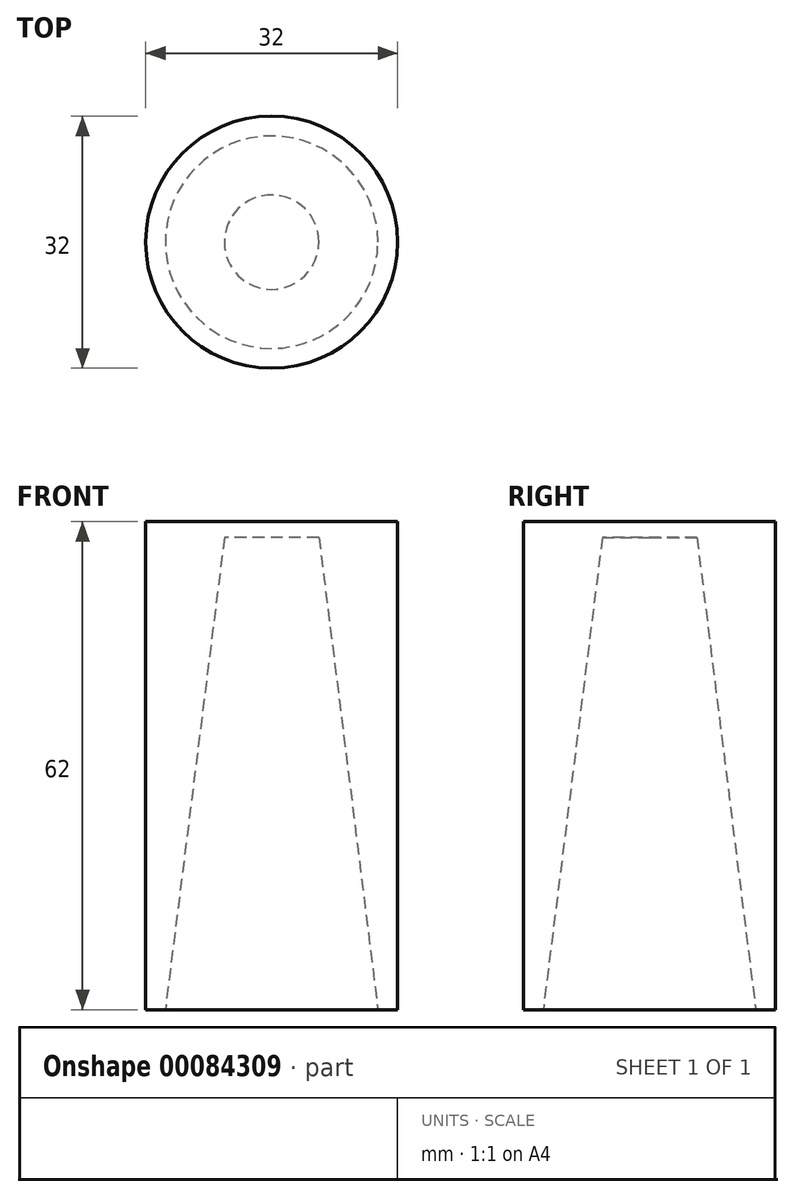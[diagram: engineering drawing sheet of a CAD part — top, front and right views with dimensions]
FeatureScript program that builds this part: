
annotation { "Feature Type Name" : "Feature", "Feature Type Description" : "" }
export const myFeature = defineFeature(function(context is Context, id is Id, definition is map)
    precondition{}
    {
        {
            var Q0;
            Q0=qCreatedBy(makeId("Top.planeOp"),FACE);
            var sketch = newSketch(context, id + "F0", { "sketchPlane" : qUnion([Q0])});
            skCircle(sketch, "E0", {"center": v(0, 0) * mm, "radius": 13.5 * mm});
            skSolve(sketch);
        }
        {
            var Q0;
            Q0=qCreatedBy(makeId("Top.planeOp"),FACE);
            cPlane(context, id + "F1", {"entities" : qUnion([Q0]), "cplaneType" : CPlaneType.OFFSET, "offset" : 60 * mm, "width" : 150 * mm, "height" : 150 * mm});
        }
        {
            var Q0;
            Q0=qCreatedBy(id+"F1.planeOp",FACE);
            var sketch = newSketch(context, id + "F2", { "sketchPlane" : qUnion([Q0])});
            skCircle(sketch, "E1", {"center": v(0, 0) * mm, "radius": 6 * mm});
            skSolve(sketch);
        }
        {
            var Q0;
            Q0=qCreatedBy(makeId("Top.planeOp"),FACE);
            var sketch = newSketch(context, id + "F3", { "sketchPlane" : qUnion([Q0])});
            skCircle(sketch, "E2", {"center": v(0, 0) * mm, "radius": 16 * mm});
            skSolve(sketch);
        }
        {
            var Q0;
            Q0=makeQuery(id+"F3.imprint","IMPRINT",FACE,{"disambiguationData":[TD([[makeQuery(id+"F3.imprint","IMPRINT",EDGE,{"derivedFrom":sQuery(id+"F3.wireOp",EDGE,"E2")}),1.0]])]});
            extrude(context, id + "F4", {"entities" : qUnion([Q0]), "depth" : 60 * mm});
        }
        {
            var Q1;
            Q1=makeQuery(id+"F2.imprint","IMPRINT",FACE,{"disambiguationData":[TD([[makeQuery(id+"F2.imprint","IMPRINT",EDGE,{"derivedFrom":sQuery(id+"F2.wireOp",EDGE,"E1")}),1.0]])]});
            var Q2;
            Q2=makeQuery(id+"F0.imprint","IMPRINT",FACE,{"disambiguationData":[TD([[makeQuery(id+"F0.imprint","IMPRINT",EDGE,{"derivedFrom":sQuery(id+"F0.wireOp",EDGE,"E0")}),1.0]])]});
            loft(context, id + "F5", {"operationType" : NewBodyOperationType.REMOVE, "sheetProfilesArray" : [{ "sheetProfileEntities" : qUnion([Q1]) }, { "sheetProfileEntities" : qUnion([Q2]) }]});
        }
        {
            var Q0;
            Q0 = qSketchRegion(id + "F2", true);
            var Q1;
            Q1=makeQuery(id+"F4.opExtrude","CAP_FACE",FACE,{"disambiguationData":[OSD([sQuery(id+"F3.wireOp",EDGE,"E2")])],"isStart":false});
            extrude(context, id + "F6", {"entities" : qUnion([Q0, Q1]), "operationType" : NewBodyOperationType.ADD, "depth" : 2 * mm});
        }
    });
